# Revit family: TZF NAO_RFA
name_source: partatom
category: Aparatos sanitarios
units: mm (PartAtom-declared; Revit-internal decimal feet)

## family parameters
Compartido = Sí
Corte con vacíos al cargar = No
Cota de conector redondo = Diámetro de uso
Número OmniClass = 23.45.05.14.31
Punto de cálculo de habitación = Sí
Se basa en plano de trabajo = Sí
Siempre vertical = Sí
Tipo de pieza = Normal
Título OmniClass = Combination Toilets

## types (1)
- TZF NAO
    Certification = https://helvex.com.mx
    Comentarios de tipo = Flush Toilet
    Compliance = NOM-009-CONAGUA-1996
    Conexión AF = Sí
    Conexión de residuos = Sí
    Descripción = 1.26 gpf Nao Flush Toilet With Exposed Trapway
    Documentation = https://helvex.com.mx
    Elevación por defecto = 0"
    Fabricante = HELVEX S.A. de C.V.
    Features = Requires 1.26 gpf Flush Valve; Sleek Ergonomic Design; Siphon Action Jetted Bowl; Flat Base; Sturdy Built; Optimum Water Surface; Maximum Efficiency; Saves On Water Consumption
    Imagen de tipo = TZF NAO.jpg
    Inlet Threads = Feeding: 15/16" - 14 NS-1; Flush: Coupled With Sanitary Flange
    Instructive = https://helvex.com.mx
    Material = High Gloss Ceramic
    Max. Working Pressure = 85.3 psi
    Min. Working Pressure = 14.2 psi
    Modelo = TZF NAO
    Total Height = 15"
    Total Length = 26"
    Total Width = 15"
    URL = https://helvex.com.mx

## geometry (parser evidence)
native form markers: Blend x4, Sweep x2
no freeform markers — native parametric forms only
